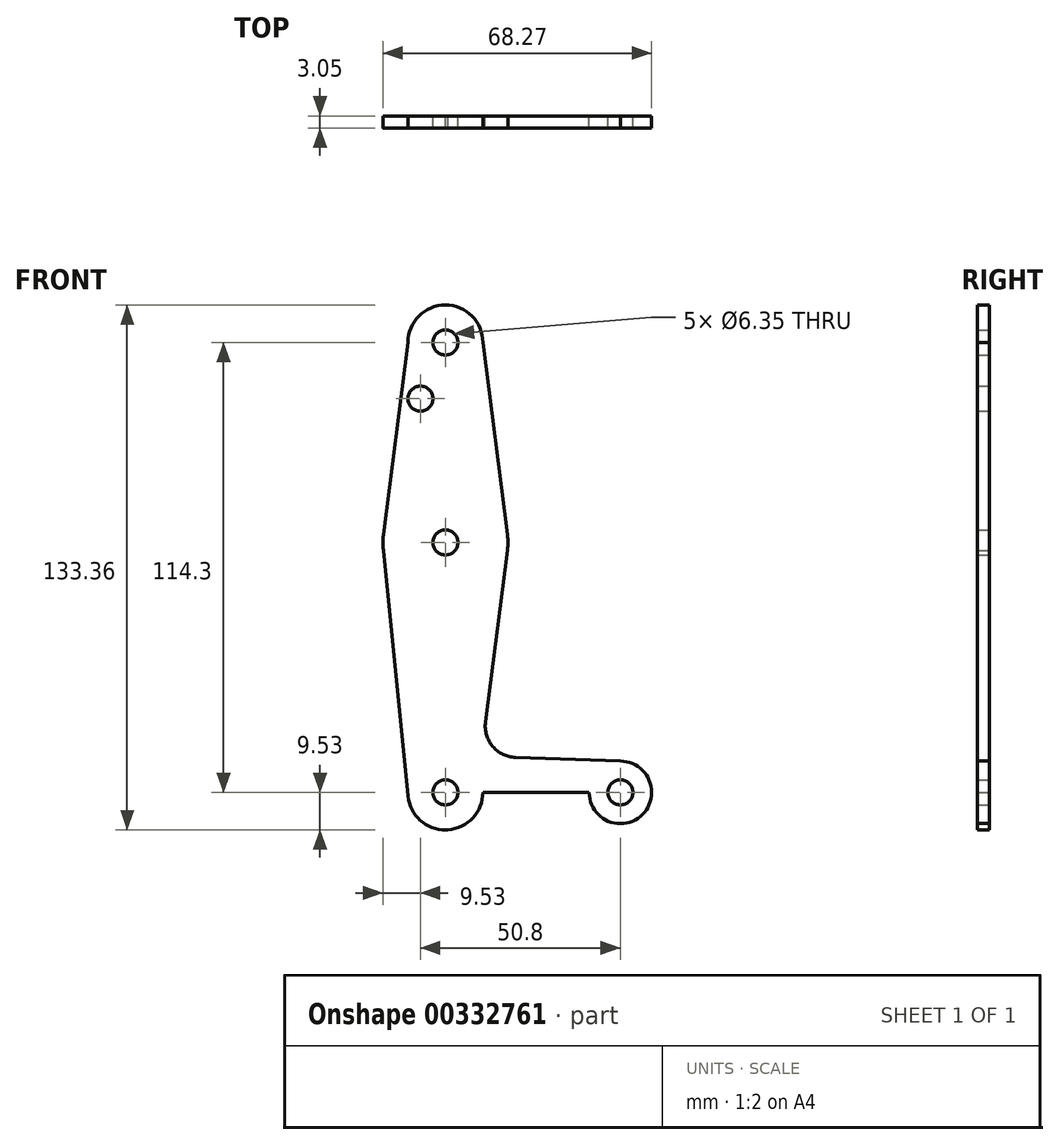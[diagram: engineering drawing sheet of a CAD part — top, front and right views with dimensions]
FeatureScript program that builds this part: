
annotation { "Feature Type Name" : "Feature", "Feature Type Description" : "" }
export const myFeature = defineFeature(function(context is Context, id is Id, definition is map)
    precondition{}
    {
        {
            var Q0;
            Q0=qCreatedBy(makeId("Front.planeOp"),FACE);
            var sketch = newSketch(context, id + "F0", { "sketchPlane" : qUnion([Q0])});
            skCircle(sketch, "E0", {"center": v(0, 0) * mm, "radius": 9.53 * mm});
            skLineSegment(sketch, "E1", {"start": v(0, 0) * mm, "end": v(44.45, 0) * mm});
            skLineSegment(sketch, "E2", {"start": v(0, 0) * mm, "end": v(0, 114.3) * mm});
            skCircle(sketch, "E3", {"center": v(0, 114.3) * mm, "radius": 9.53 * mm});
            skCircle(sketch, "E4", {"center": v(44.45, 0) * mm, "radius": 7.94 * mm});
            skCircle(sketch, "E5", {"center": v(0, 63.5) * mm, "radius": 15.88 * mm});
            skLineSegment(sketch, "E6", {"start": v(0, -9.52) * mm, "end": v(44.45, -7.94) * mm});
            skLineSegment(sketch, "E7", {"start": v(44.45, 7.94) * mm, "end": v(17.78, 8.9) * mm});
            skLineSegment(sketch, "E8", {"start": v(-9.53, 114.3) * mm, "end": v(-15.75, 65.5) * mm});
            skLineSegment(sketch, "E9", {"start": v(9.53, 114.3) * mm, "end": v(15.75, 65.5) * mm});
            skLineSegment(sketch, "E10", {"start": v(-15.75, 61.5) * mm, "end": v(-9.48, -0.95) * mm});
            skLineSegment(sketch, "E11", {"start": v(15.75, 61.5) * mm, "end": v(10.18, 17.84) * mm});
            skCircle(sketch, "E12", {"center": v(0, 114.3) * mm, "radius": 3.18 * mm});
            skCircle(sketch, "E13", {"center": v(0, 63.5) * mm, "radius": 3.18 * mm});
            skCircle(sketch, "E14", {"center": v(0, 0) * mm, "radius": 3.18 * mm});
            skCircle(sketch, "E15", {"center": v(44.45, 0) * mm, "radius": 3.18 * mm});
            skCircle(sketch, "E16", {"center": v(-6.35, 100.03) * mm, "radius": 3.18 * mm});
            skPoint(sketch, "E17.newPointA", {"position": v(7.78, -0.95) * mm});
            skArc(sketch, "E17.filletArc", {"start": v(10.18, 17.84) * mm, "mid": v(12, 11.7) * mm, "end": v(17.78, 8.9) * mm});
            skSolve(sketch);
        }
        {
            var Q0;
            {var subQ0=sQuery(id+"F0.wireOp",EDGE,"E6");var subQ1=sQuery(id+"F0.wireOp",EDGE,"E0");var subQ2=makeQuery(id+"F0.imprint","INTERSECT",VERTEX,{"disambiguationData":[OD(0.0)],"derivedFrom":[subQ1,subQ0]});Q0=makeQuery(id+"F0.imprint","IMPRINT",FACE,{"disambiguationData":[TD([[makeQuery(id+"F0.imprint","IMPRINT",EDGE,{"disambiguationData":[TD([[subQ2,-1.0]])],"derivedFrom":subQ1}),1.0]])]});}
            var Q1;
            {var subQ0=sQuery(id+"F0.wireOp",EDGE,"E10");Q1=makeQuery(id+"F0.imprint","IMPRINT",FACE,{"disambiguationData":[TD([[makeQuery(id+"F0.imprint","IMPRINT",EDGE,{"derivedFrom":subQ0}),1.0]])]});}
            var Q2;
            {var subQ0=sQuery(id+"F0.wireOp",EDGE,"E6");var subQ1=sQuery(id+"F0.wireOp",EDGE,"E0");var subQ2=makeQuery(id+"F0.imprint","INTERSECT",VERTEX,{"disambiguationData":[OD(1.0)],"derivedFrom":[subQ1,subQ0]});Q2=makeQuery(id+"F0.imprint","IMPRINT",FACE,{"disambiguationData":[TD([[makeQuery(id+"F0.imprint","IMPRINT",EDGE,{"disambiguationData":[TD([[subQ2,-1.0]])],"derivedFrom":subQ1}),-1.0]])]});}
            var Q3;
            {var subQ5=sQuery(id+"F0.wireOp",EDGE,"E9");Q3=makeQuery(id+"F0.imprint","IMPRINT",FACE,{"disambiguationData":[TD([[makeQuery(id+"F0.imprint","IMPRINT",EDGE,{"derivedFrom":subQ5}),-1.0]])]});}
            var Q4;
            Q4=makeQuery(id+"F0.imprint","IMPRINT",FACE,{"disambiguationData":[TD([[makeQuery(id+"F0.imprint","IMPRINT",EDGE,{"derivedFrom":sQuery(id+"F0.wireOp",EDGE,"E12")}),-1.0]])]});
            var Q5;
            Q5=makeQuery(id+"F0.imprint","IMPRINT",FACE,{"disambiguationData":[TD([[makeQuery(id+"F0.imprint","IMPRINT",EDGE,{"derivedFrom":sQuery(id+"F0.wireOp",EDGE,"E15")}),-1.0]])]});
            var Q6;
            {var subQ0=sQuery(id+"F0.wireOp",EDGE,"E5");var subQ2=sQuery(id+"F0.wireOp",EDGE,"E2");var subQ3=makeQuery(id+"F0.imprint","INTERSECT",VERTEX,{"disambiguationData":[OD(0.0)],"derivedFrom":[subQ2,subQ0]});Q6=makeQuery(id+"F0.imprint","IMPRINT",FACE,{"disambiguationData":[TD([[makeQuery(id+"F0.imprint","IMPRINT",EDGE,{"disambiguationData":[TD([[subQ3,-1.0]])],"derivedFrom":subQ2}),-1.0]])]});}
            var Q7;
            {var subQ0=sQuery(id+"F0.wireOp",EDGE,"E5");var subQ2=sQuery(id+"F0.wireOp",EDGE,"E2");var subQ4=makeQuery(id+"F0.imprint","INTERSECT",VERTEX,{"disambiguationData":[OD(0.0)],"derivedFrom":[subQ2,subQ0]});Q7=makeQuery(id+"F0.imprint","IMPRINT",FACE,{"disambiguationData":[TD([[makeQuery(id+"F0.imprint","IMPRINT",EDGE,{"disambiguationData":[TD([[subQ4,-1.0]])],"derivedFrom":subQ2}),1.0]])]});}
            var Q8;
            {var subQ0=sQuery(id+"F0.wireOp",EDGE,"E8");Q8=makeQuery(id+"F0.imprint","IMPRINT",FACE,{"disambiguationData":[TD([[makeQuery(id+"F0.imprint","IMPRINT",EDGE,{"derivedFrom":subQ0}),1.0]])]});}
            var Q9;
            {var subQ0=sQuery(id+"F0.wireOp",EDGE,"E7");Q9=makeQuery(id+"F0.imprint","IMPRINT",FACE,{"disambiguationData":[TD([[makeQuery(id+"F0.imprint","IMPRINT",EDGE,{"derivedFrom":subQ0}),1.0]])]});}
            var Q10;
            {var subQ1=sQuery(id+"F0.wireOp",EDGE,"E0");var subQ6=makeQuery(id+"F0.imprint","INTERSECT",VERTEX,{"derivedFrom":[subQ1,sQuery(id+"F0.wireOp",EDGE,"E10")]});Q10=makeQuery(id+"F0.imprint","IMPRINT",FACE,{"disambiguationData":[TD([[makeQuery(id+"F0.imprint","IMPRINT",EDGE,{"disambiguationData":[TD([[subQ6,1.0]])],"derivedFrom":subQ1}),1.0]])]});}
            var Q11;
            {var subQ0=sQuery(id+"F0.wireOp",EDGE,"E2");var subQ1=sQuery(id+"F0.wireOp",EDGE,"E0");var subQ2=makeQuery(id+"F0.imprint","INTERSECT",VERTEX,{"derivedFrom":[subQ1,subQ0]});Q11=makeQuery(id+"F0.imprint","IMPRINT",FACE,{"disambiguationData":[TD([[makeQuery(id+"F0.imprint","IMPRINT",EDGE,{"disambiguationData":[TD([[subQ2,1.0]])],"derivedFrom":subQ1}),1.0]])]});}
            extrude(context, id + "F1", {"entities" : qUnion([Q0, Q1, Q2, Q3, Q4, Q5, Q6, Q7, Q8, Q9, Q10, Q11]), "depth" : 3.05 * mm});
        }
    });
